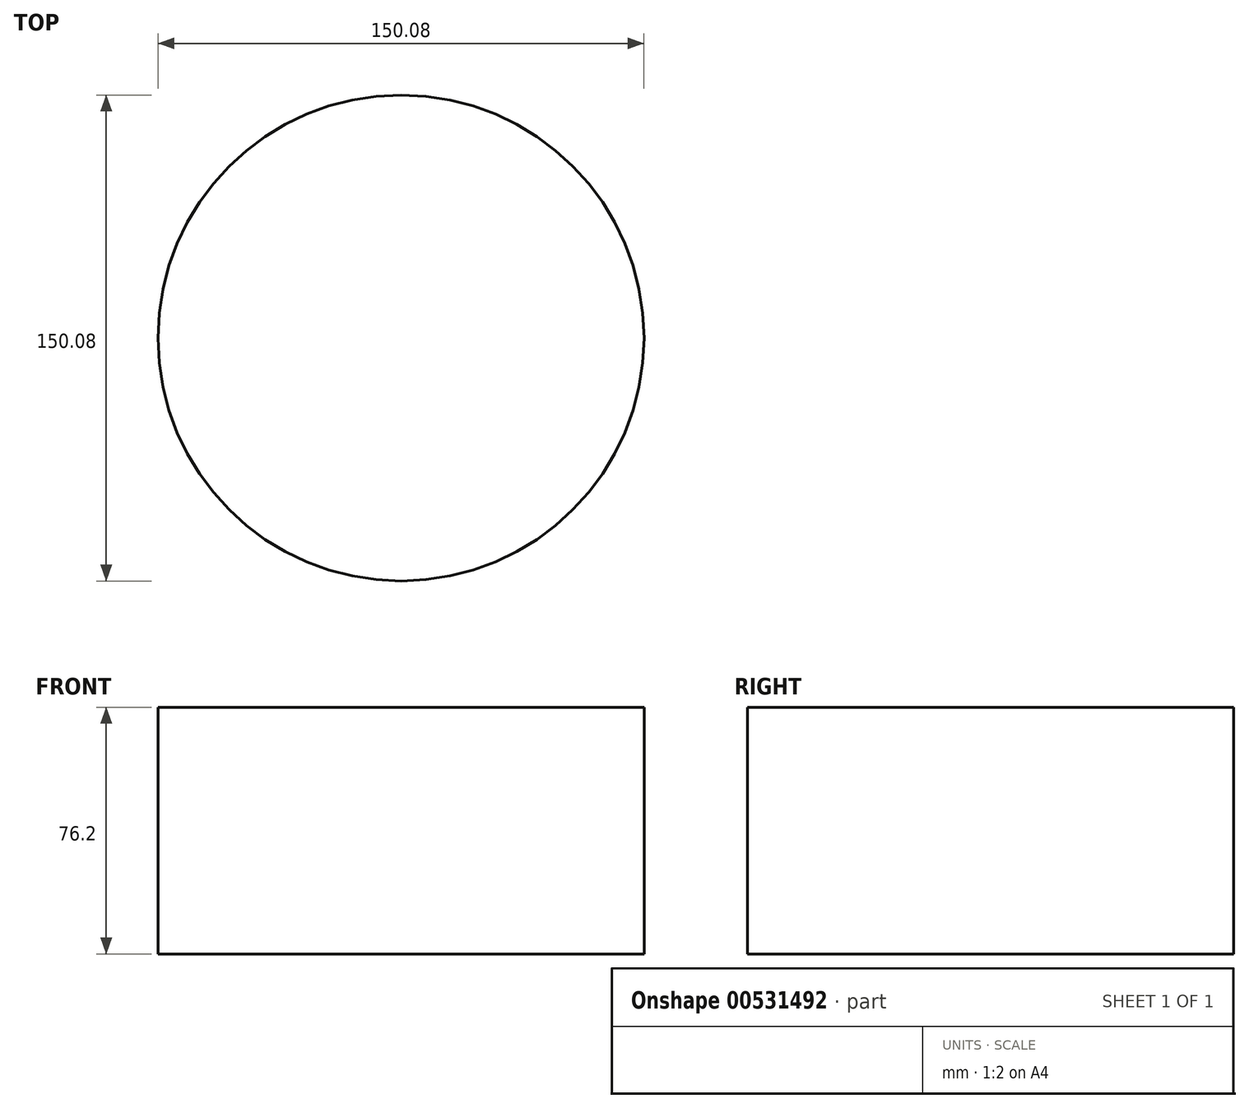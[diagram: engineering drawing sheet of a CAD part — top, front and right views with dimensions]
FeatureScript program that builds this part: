
annotation { "Feature Type Name" : "Feature", "Feature Type Description" : "" }
export const myFeature = defineFeature(function(context is Context, id is Id, definition is map)
    precondition{}
    {
        {
            var Q0;
            Q0=qCreatedBy(makeId("Top.planeOp"),FACE);
            var sketch = newSketch(context, id + "F0", { "sketchPlane" : qUnion([Q0])});
            skCircle(sketch, "E0", {"center": v(0, 0) * mm, "radius": 75.04 * mm});
            skSolve(sketch);
        }
        {
            var Q0;
            Q0=sQuery(id+"F0.wireOp",EDGE,"E0");
            extrude(context, id + "F1", {"bodyType" : ToolBodyType.SURFACE, "surfaceEntities" : qUnion([Q0]), "depth" : 76.2 * mm, "offsetDistance" : 25.4 * mm});
        }
    });
